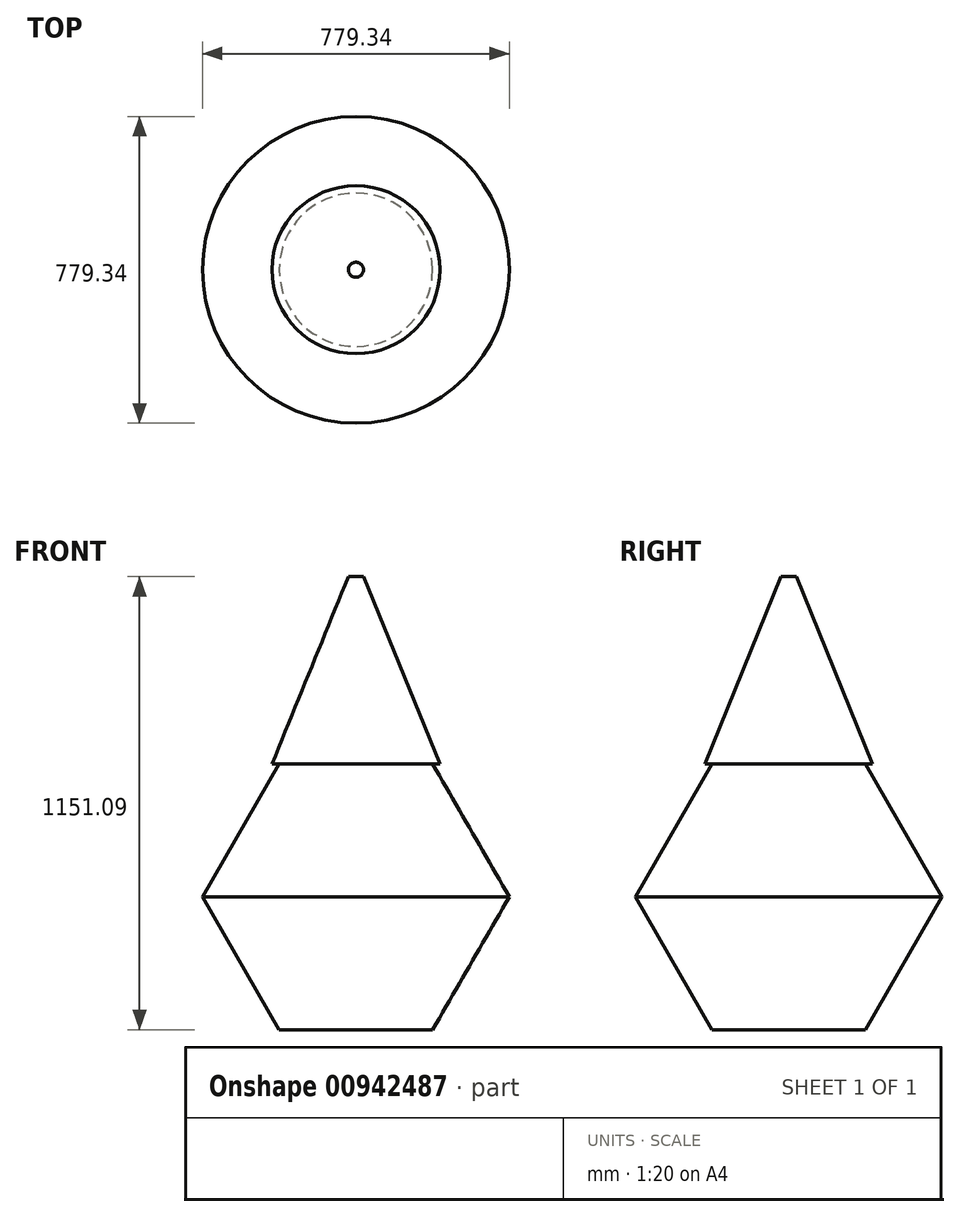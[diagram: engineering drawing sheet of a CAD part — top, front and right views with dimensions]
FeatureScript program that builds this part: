
annotation { "Feature Type Name" : "Feature", "Feature Type Description" : "" }
export const myFeature = defineFeature(function(context is Context, id is Id, definition is map)
    precondition{}
    {
        {
            var Q0;
            Q0=qCreatedBy(makeId("Front.planeOp"),FACE);
            var sketch = newSketch(context, id + "F0", { "sketchPlane" : qUnion([Q0])});
            skLineSegment(sketch, "E0", {"start": v(0, 0) * mm, "end": v(0, 609.6) * mm});
            skLineSegment(sketch, "E1", {"start": v(-304.8, 0) * mm, "end": v(0, 0) * mm});
            skLineSegment(sketch, "E2", {"start": v(0, 609.6) * mm, "end": v(0, 680.23) * mm});
            skLineSegment(sketch, "E3", {"start": v(0, 680.23) * mm, "end": v(-27.39, 680.23) * mm});
            skLineSegment(sketch, "E4", {"start": v(-27.39, 680.23) * mm, "end": v(-304.8, 0) * mm});
            skSolve(sketch);
        }
        {
            var Q0;
            Q0=makeQuery(id+"F0.imprint","IMPRINT",FACE,{"disambiguationData":[TD([[makeQuery(id+"F0.imprint","IMPRINT",EDGE,{"derivedFrom":sQuery(id+"F0.wireOp",EDGE,"E0")}),1.0]])]});
            var Q1;
            Q1=sQuery(id+"F0.wireOp",EDGE,"E0");
            revolve(context, id + "F1", {"surfaceOperationType" : NewSurfaceOperationType.NEW, "entities" : qUnion([Q0]), "axis" : qUnion([Q1]), "revolveType" : RevolveType.FULL});
        }
        {
            var Q0;
            Q0=qCreatedBy(makeId("Right.planeOp"),FACE);
            var sketch = newSketch(context, id + "F2", { "sketchPlane" : qUnion([Q0])});
            skArc(sketch, "E5.cCircle", {"start": v(0, 0) * mm, "mid": v(-482.1, -482.1) * mm, "end": v(0, -964.18) * mm, "construction": true});
            skLineSegment(sketch, "E5.0", {"start": v(-278.34, 0) * mm, "end": v(0, 0) * mm});
            skLineSegment(sketch, "E5.3", {"start": v(0, -964.18) * mm, "end": v(-278.34, -964.18) * mm});
            skLineSegment(sketch, "E5.4", {"start": v(-278.34, -964.18) * mm, "end": v(-556.67, -482.1) * mm});
            skLineSegment(sketch, "E5.5", {"start": v(-556.67, -482.1) * mm, "end": v(-278.34, 0) * mm});
            skPoint(sketch, "E5.0.midPoint", {"position": v(0, 0) * mm});
            skLineSegment(sketch, "E6", {"start": v(0, 0) * mm, "end": v(0, -964.18) * mm});
            skPoint(sketch, "E7.orphan", {"position": v(278.34, 0) * mm});
            skPoint(sketch, "E5.2.end.orphan", {"position": v(278.34, -964.18) * mm});
            skSolve(sketch);
        }
        {
            var Q0;
            Q0 = qSketchRegion(id + "F2", true);
            var Q1;
            Q1 = qSketchRegion(id + "F4", true);
            var Q2;
            Q2=sQuery(id+"F2.wireOp",EDGE,"E6");
            revolve(context, id + "F3", {"operationType" : NewBodyOperationType.ADD, "surfaceOperationType" : NewSurfaceOperationType.NEW, "entities" : qUnion([Q0, Q1]), "axis" : qUnion([Q2]), "revolveType" : RevolveType.FULL});
        }
        {
            var Q0;
            Q0=qCreatedBy(makeId("Top.planeOp"),FACE);
            var sketch = newSketch(context, id + "F4", { "sketchPlane" : qUnion([Q0])});
            skCircle(sketch, "E8", {"center": v(0, 0) * mm, "radius": 86.27 * mm});
            skSolve(sketch);
        }
        {
            var Q0;
            Q0=sQuery(id+"F4.wireOp",EDGE,"E8");
            extrude(context, id + "F5", {"bodyType" : ToolBodyType.SURFACE, "surfaceEntities" : qUnion([Q0]), "oppositeDirection" : true, "depth" : 1381.76 * mm, "offsetDistance" : 25.4 * mm});
        }
        {
            var Q0;
            Q0=makeQuery(id+"F1.opRevolve","SWEPT_BODY",BODY,{"disambiguationData":[OSD([sQuery(id+"F0.wireOp",EDGE,"E0"),sQuery(id+"F0.wireOp",EDGE,"E1"),sQuery(id+"F0.wireOp",EDGE,"E2"),sQuery(id+"F0.wireOp",EDGE,"E3"),sQuery(id+"F0.wireOp",EDGE,"E4")])]});
            var Q1;
            Q1=makeQuery(id+"F5.opExtrude","SWEPT_BODY",BODY,{"disambiguationData":[OSD([sQuery(id+"F4.wireOp",EDGE,"E8")])]});
            var Q2;
            Q2=qCreatedBy(makeId("Origin.pointOp"),VERTEX);
            transform(context, id + "F6", {"entities" : qUnion([Q0, Q1]), "transformType" : TransformType.SCALE_UNIFORMLY, "scale" : .7, "scalePoint" : qUnion([Q2]), "makeCopy" : false});
        }
    });
